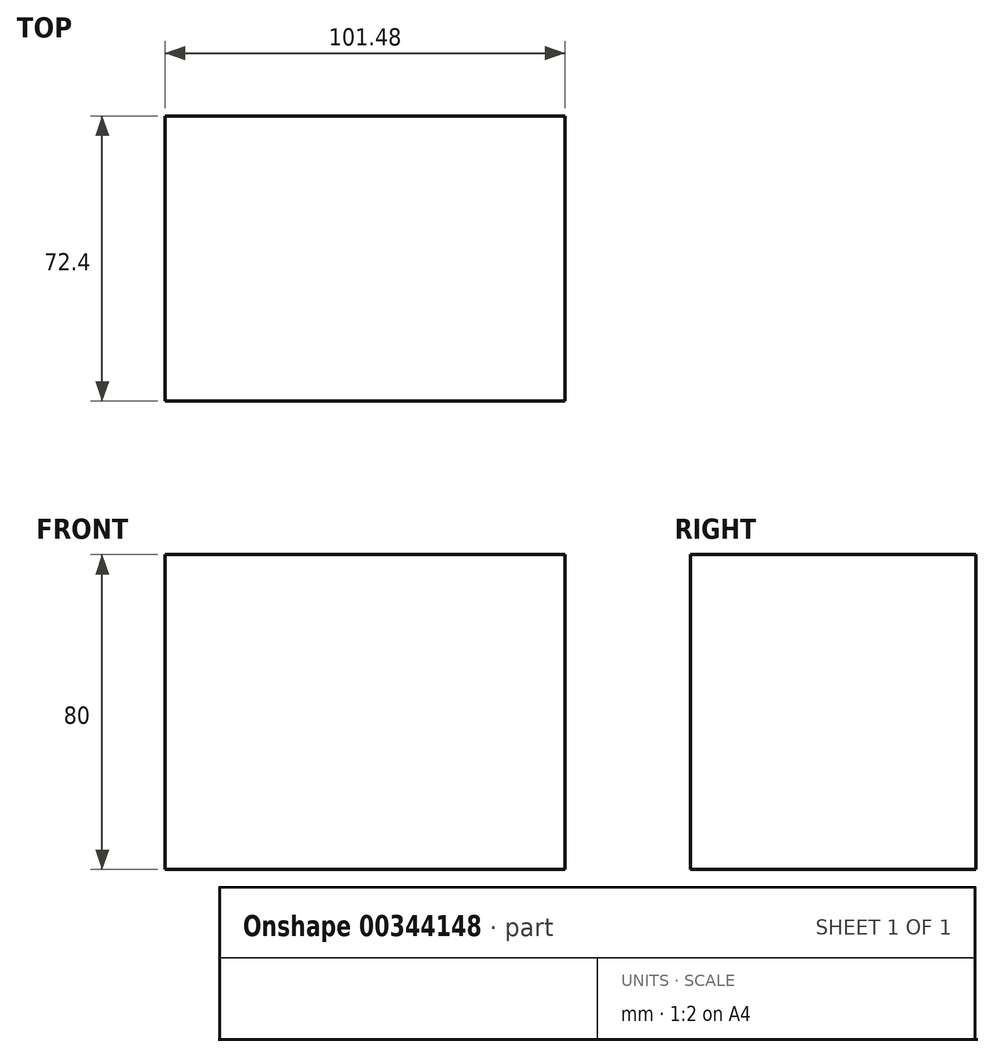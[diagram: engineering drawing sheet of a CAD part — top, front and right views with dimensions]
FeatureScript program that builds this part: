
annotation { "Feature Type Name" : "Feature", "Feature Type Description" : "" }
export const myFeature = defineFeature(function(context is Context, id is Id, definition is map)
    precondition{}
    {
        {
            var Q0;
            Q0=qCreatedBy(makeId("Top.planeOp"),FACE);
            var sketch = newSketch(context, id + "F0", { "sketchPlane" : qUnion([Q0])});
            skLineSegment(sketch, "E0.bottom", {"start": v(50.74, 36.2) * mm, "end": v(-50.74, 36.2) * mm});
            skLineSegment(sketch, "E0.top", {"start": v(50.74, -36.2) * mm, "end": v(-50.74, -36.2) * mm});
            skLineSegment(sketch, "E0.left", {"start": v(50.74, 36.2) * mm, "end": v(50.74, -36.2) * mm});
            skLineSegment(sketch, "E0.right", {"start": v(-50.74, 36.2) * mm, "end": v(-50.74, -36.2) * mm});
            skPoint(sketch, "E0.middle", {"position": v(0, 0) * mm});
            skSolve(sketch);
        }
        {
            var Q0;
            Q0=makeQuery(id+"F0.imprint","IMPRINT",FACE,{"disambiguationData":[TD([[makeQuery(id+"F0.imprint","IMPRINT",EDGE,{"derivedFrom":sQuery(id+"F0.wireOp",EDGE,"E0.bottom")}),1.0]])]});
            extrude(context, id + "F1", {"entities" : qUnion([Q0]), "depth" : 80 * mm});
        }
    });
